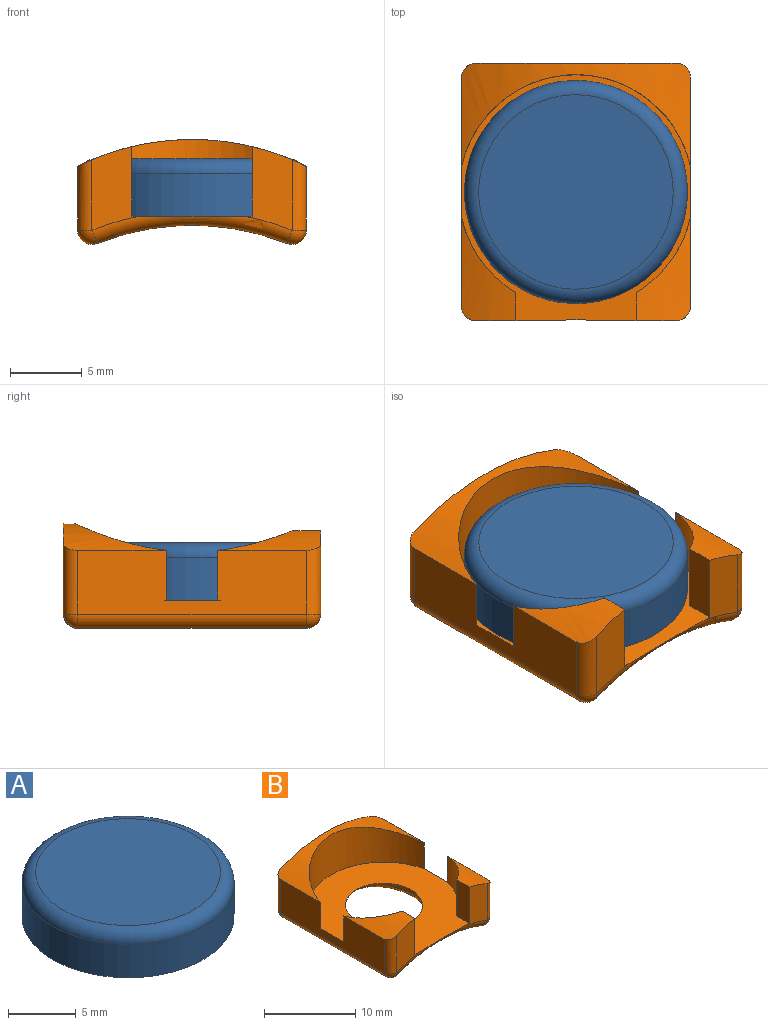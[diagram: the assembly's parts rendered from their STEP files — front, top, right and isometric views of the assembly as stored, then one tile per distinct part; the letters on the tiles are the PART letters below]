
ASSEMBLY  parts=2 mates=1
PART A: 4 faces, bbox 16.9x16.9x4 mm
  f0: cylinder r=7.8mm len=15.6mm, axis (0,0,-1), area 147mm2, adj f2,f3
  f1: plane 13.6x13.6mm, normal (0,0,1), area 145.3mm2, adj f3
  f2: plane 15.6x15.6mm, normal (0,0,-1), area 191.1mm2, adj f0
  f3: torus R=6.8mm, axis (0,0,1), area 73.4mm2, adj f0,f1
PART B: 30 faces, bbox 16.7x18.7x8.1 mm
  f0: cylinder r=4.2mm len=5.97mm, axis (0,0,1), area 1.2mm2, adj f1,f29
  f1: plane 17.92x16.72mm, normal (0,0,1), area 164mm2, adj f0,f2,f19,f20,f21,f22,f23,f24
  f2: plane 4.86x1.96mm, normal (1,0,0), area 9.5mm2, adj f1,f3,f19,f27
  f3: cylinder r=18mm len=7.2mm, axis (0,1,0), area 18mm2, adj f2,f4,f19,f20,f27
  f4: cylinder r=1mm len=4.92mm, axis (0,0,1), area 7.4mm2, adj f3,f5,f20,f27
  f5: sphere r=1mm, area 1.9mm2, adj f4,f6,f26
  f6: cylinder r=1mm len=16mm, axis (0,1,0), area 31.2mm2, adj f5,f7,f18,f20
  f7: cylinder r=18mm len=16mm, axis (0,1,0), area 136.1mm2, adj f6,f8,f14,f26,f29
  f8: torus R=19mm, axis (0,-1,0), area 21.8mm2, adj f7,f9,f13,f18
  f9: sphere r=1mm, area 2.4mm2, adj f8,f10,f14
  f10: cylinder r=1mm len=4.92mm, axis (0,0,1), area 7.4mm2, adj f9,f11,f13,f22
  f11: cylinder r=18mm len=16mm, axis (0,1,0), area 40.1mm2, adj f10,f12,f13,f20,f21,f22
  f12: cylinder r=1mm len=4.92mm, axis (0,0,-1), area 7.4mm2, adj f11,f13,f18,f20
  f13: plane 14x6.34mm, normal (0,1,0), area 69.6mm2, adj f8,f10,f11,f12
  f14: cylinder r=1mm len=16mm, axis (0,1,0), area 31.2mm2, adj f7,f9,f15,f22
  f15: sphere r=1mm, area 1.9mm2, adj f14,f16,f26
  f16: cylinder r=1mm len=4.92mm, axis (0,0,-1), area 7.4mm2, adj f15,f17,f22,f25
  f17: cylinder r=18mm len=7.2mm, axis (0,1,0), area 18mm2, adj f16,f22,f23,f24,f25
  f18: sphere r=1mm, area 1.3mm2, adj f6,f8,f12
  f19: cylinder r=8.2mm len=5.24mm, axis (0,0,1), area 27.8mm2, adj f1,f2,f3,f20
  f20: plane 16x4.46mm, normal (-1,0,0), area 58.8mm2, adj f1,f3,f4,f6,f11,f12,f19,f21
  f21: cylinder r=8.2mm len=16mm, axis (0,0,1), area 100.5mm2, adj f1,f11,f20,f22
  f22: plane 16x4.46mm, normal (1,0,0), area 58.8mm2, adj f1,f10,f11,f14,f16,f17,f21,f23
  f23: cylinder r=8.2mm len=5.24mm, axis (0,0,1), area 27.8mm2, adj f1,f17,f22,f24
  f24: plane 4.86x1.96mm, normal (-1,0,0), area 9.5mm2, adj f1,f17,f23,f25
  f25: plane 5.84x3.34mm, normal (0,-1,0), area 13.9mm2, adj f1,f16,f17,f24,f26
  f26: torus R=19mm, axis (0,-1,0), area 20mm2, adj f1,f5,f7,f15,f25,f27
  f27: plane 5.84x3.34mm, normal (0,-1,0), area 13.9mm2, adj f1,f2,f3,f4,f26
  f28: cylinder r=4.2mm len=5.97mm, axis (0,0,1), area 0mm2, adj f1,f29
  f29: bspline ~10.41x9.86mm, area 40.8mm2, adj f0,f1,f7,f28
PLACE A t=(0,0,-49.5)mm
PLACE B at identity
MATE planar A.f0 <-> B.f0  axis (0,0,-1) through (0,0,0.5)mm
